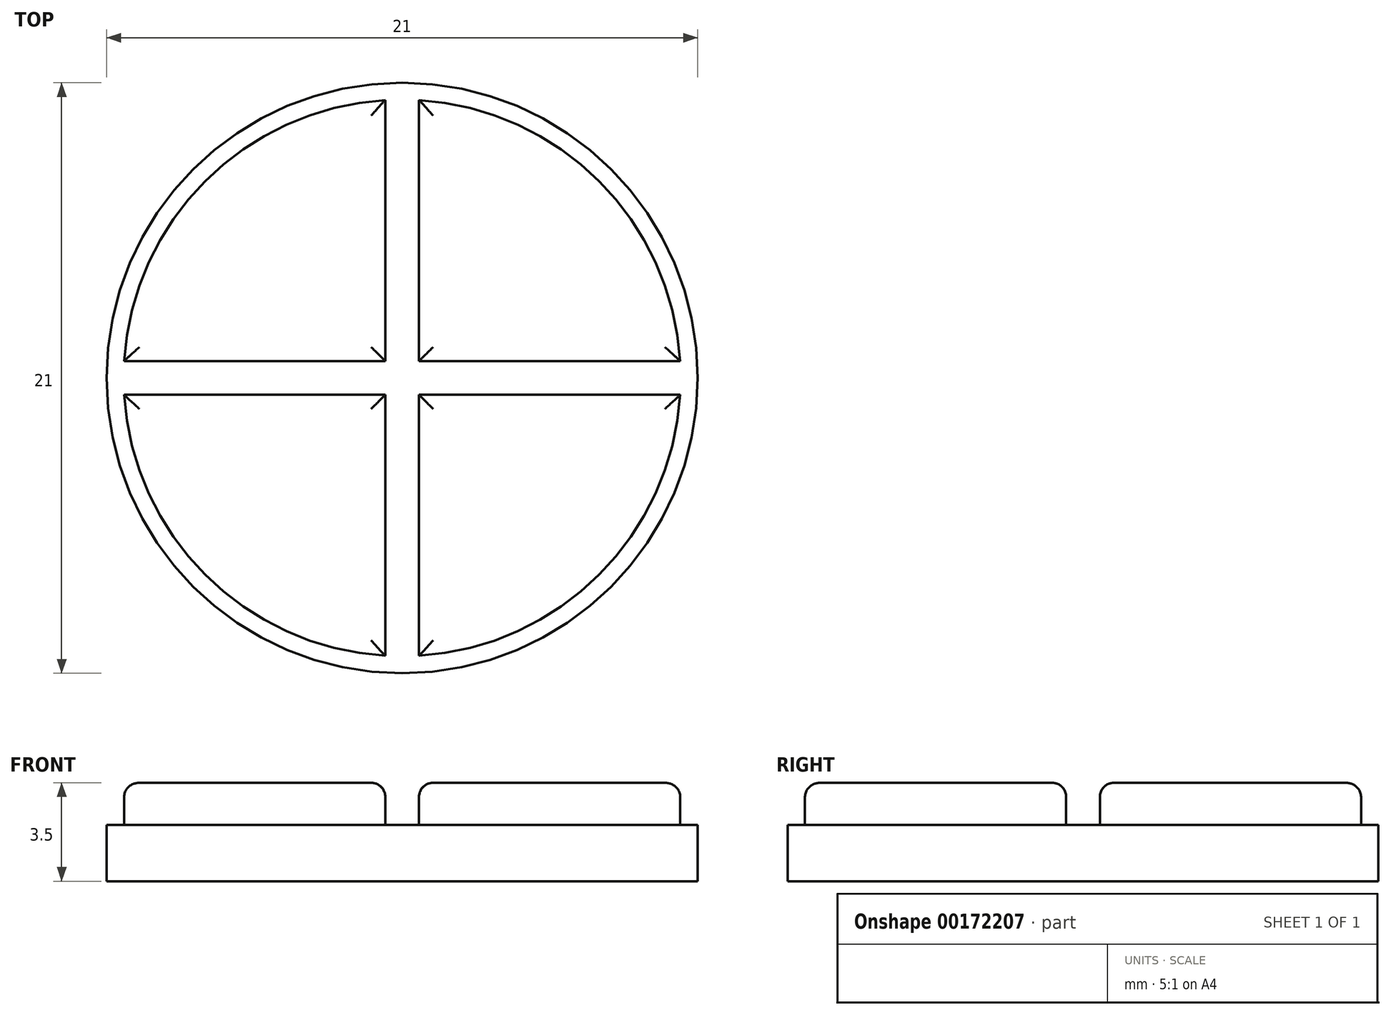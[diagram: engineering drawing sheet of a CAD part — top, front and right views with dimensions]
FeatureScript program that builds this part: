
annotation { "Feature Type Name" : "Feature", "Feature Type Description" : "" }
export const myFeature = defineFeature(function(context is Context, id is Id, definition is map)
    precondition{}
    {
        {
            var Q0;
            Q0=qCreatedBy(makeId("Top.planeOp"),FACE);
            var sketch = newSketch(context, id + "F0", { "sketchPlane" : qUnion([Q0])});
            skCircle(sketch, "E0", {"center": v(0, 0) * mm, "radius": 10.5 * mm});
            skSolve(sketch);
        }
        {
            var Q0;
            Q0=qSketchRegion(id+"F0",true);
            extrude(context, id + "F1", {"entities" : qUnion([Q0]), "depth" : 2 * mm});
        }
        {
            var Q0;
            Q0=makeQuery(id+"F1.opExtrude","CAP_FACE",FACE,{"disambiguationData":[OSD([sQuery(id+"F0.wireOp",EDGE,"E0")])],"isStart":false});
            var sketch = newSketch(context, id + "F2", { "sketchPlane" : qUnion([Q0])});
            skCircle(sketch, "E1", {"center": v(0, 0) * mm, "radius": 9.9 * mm});
            skLineSegment(sketch, "E2.bottom", {"start": v(9.88, -0.6) * mm, "end": v(-9.88, -0.6) * mm});
            skLineSegment(sketch, "E2.top", {"start": v(9.88, 0.6) * mm, "end": v(-9.88, 0.6) * mm});
            skLineSegment(sketch, "E2.left", {"start": v(9.88, -0.6) * mm, "end": v(9.88, 0.6) * mm});
            skLineSegment(sketch, "E2.right", {"start": v(-9.88, -0.6) * mm, "end": v(-9.88, 0.6) * mm});
            skLineSegment(sketch, "E3.bottom", {"start": v(0.6, -9.88) * mm, "end": v(-0.6, -9.88) * mm});
            skLineSegment(sketch, "E3.top", {"start": v(0.6, 9.88) * mm, "end": v(-0.6, 9.88) * mm});
            skLineSegment(sketch, "E3.left", {"start": v(0.6, -9.88) * mm, "end": v(0.6, 9.88) * mm});
            skLineSegment(sketch, "E3.right", {"start": v(-0.6, -9.88) * mm, "end": v(-0.6, 9.88) * mm});
            skSolve(sketch);
        }
        {
            var Q0;
            {var subQ0=sQuery(id+"F2.wireOp",EDGE,"E2.bottom");var subQ3=sQuery(id+"F2.wireOp",EDGE,"E3.right");var subQ5=makeQuery(id+"F2.imprint","INTERSECT",VERTEX,{"derivedFrom":[subQ0,subQ3]});Q0=makeQuery(id+"F2.imprint","IMPRINT",FACE,{"disambiguationData":[TD([[makeQuery(id+"F2.imprint","IMPRINT",EDGE,{"disambiguationData":[TD([[subQ5,-1.0]])],"derivedFrom":subQ0}),1.0]])]});}
            var Q1;
            {var subQ0=sQuery(id+"F2.wireOp",EDGE,"E2.top");var subQ3=sQuery(id+"F2.wireOp",EDGE,"E3.right");var subQ5=makeQuery(id+"F2.imprint","INTERSECT",VERTEX,{"derivedFrom":[subQ0,subQ3]});Q1=makeQuery(id+"F2.imprint","IMPRINT",FACE,{"disambiguationData":[TD([[makeQuery(id+"F2.imprint","IMPRINT",EDGE,{"disambiguationData":[TD([[subQ5,-1.0]])],"derivedFrom":subQ0}),-1.0]])]});}
            var Q2;
            {var subQ0=sQuery(id+"F2.wireOp",EDGE,"E2.top");var subQ3=sQuery(id+"F2.wireOp",EDGE,"E3.left");var subQ5=makeQuery(id+"F2.imprint","INTERSECT",VERTEX,{"derivedFrom":[subQ0,subQ3]});Q2=makeQuery(id+"F2.imprint","IMPRINT",FACE,{"disambiguationData":[TD([[makeQuery(id+"F2.imprint","IMPRINT",EDGE,{"disambiguationData":[TD([[subQ5,1.0]])],"derivedFrom":subQ0}),-1.0]])]});}
            var Q3;
            {var subQ0=sQuery(id+"F2.wireOp",EDGE,"E2.bottom");var subQ3=sQuery(id+"F2.wireOp",EDGE,"E3.left");var subQ5=makeQuery(id+"F2.imprint","INTERSECT",VERTEX,{"derivedFrom":[subQ0,subQ3]});Q3=makeQuery(id+"F2.imprint","IMPRINT",FACE,{"disambiguationData":[TD([[makeQuery(id+"F2.imprint","IMPRINT",EDGE,{"disambiguationData":[TD([[subQ5,1.0]])],"derivedFrom":subQ0}),1.0]])]});}
            extrude(context, id + "F3", {"entities" : qUnion([Q0, Q1, Q2, Q3]), "operationType" : NewBodyOperationType.ADD, "depth" : 1.5 * mm});
        }
        {
            var Q0;
            {var subQ0=sQuery(id+"F2.wireOp",EDGE,"E1");Q0=makeQuery(id+"F3.opExtrude","CAP_EDGE",EDGE,{"disambiguationData":[OSD([subQ0]),TDD([makeQuery(id+"F2.imprint","IMPRINT",EDGE,{"disambiguationData":[TD([[makeQuery(id+"F2.imprint","INTERSECT",VERTEX,{"derivedFrom":[subQ0,sQuery(id+"F2.wireOp",EDGE,"E2.bottom"),sQuery(id+"F2.wireOp",EDGE,"E2.right")]}),-1.0]])],"derivedFrom":subQ0})])],"isStart":false});}
            var Q1;
            {var subQ0=sQuery(id+"F2.wireOp",EDGE,"E3.right");Q1=makeQuery(id+"F3.opExtrude","CAP_EDGE",EDGE,{"disambiguationData":[OSD([subQ0]),TDD([makeQuery(id+"F2.imprint","IMPRINT",EDGE,{"disambiguationData":[TD([[makeQuery(id+"F2.imprint","INTERSECT",VERTEX,{"derivedFrom":[sQuery(id+"F2.wireOp",EDGE,"E2.bottom"),subQ0]}),1.0]])],"derivedFrom":subQ0})])],"isStart":false});}
            var Q2;
            {var subQ0=sQuery(id+"F2.wireOp",EDGE,"E2.bottom");Q2=makeQuery(id+"F3.opExtrude","CAP_EDGE",EDGE,{"disambiguationData":[OSD([subQ0]),TDD([makeQuery(id+"F2.imprint","IMPRINT",EDGE,{"disambiguationData":[TD([[makeQuery(id+"F2.imprint","INTERSECT",VERTEX,{"derivedFrom":[subQ0,sQuery(id+"F2.wireOp",EDGE,"E3.right")]}),-1.0]])],"derivedFrom":subQ0})])],"isStart":false});}
            var Q3;
            {var subQ0=sQuery(id+"F2.wireOp",EDGE,"E2.top");Q3=makeQuery(id+"F3.opExtrude","CAP_EDGE",EDGE,{"disambiguationData":[OSD([subQ0]),TDD([makeQuery(id+"F2.imprint","IMPRINT",EDGE,{"disambiguationData":[TD([[makeQuery(id+"F2.imprint","INTERSECT",VERTEX,{"derivedFrom":[subQ0,sQuery(id+"F2.wireOp",EDGE,"E3.right")]}),-1.0]])],"derivedFrom":subQ0})])],"isStart":false});}
            var Q4;
            {var subQ0=sQuery(id+"F2.wireOp",EDGE,"E3.right");Q4=makeQuery(id+"F3.opExtrude","CAP_EDGE",EDGE,{"disambiguationData":[OSD([subQ0]),TDD([makeQuery(id+"F2.imprint","IMPRINT",EDGE,{"disambiguationData":[TD([[makeQuery(id+"F2.imprint","INTERSECT",VERTEX,{"derivedFrom":[sQuery(id+"F2.wireOp",EDGE,"E2.top"),subQ0]}),-1.0]])],"derivedFrom":subQ0})])],"isStart":false});}
            var Q5;
            {var subQ0=sQuery(id+"F2.wireOp",EDGE,"E2.top");Q5=makeQuery(id+"F3.opExtrude","CAP_EDGE",EDGE,{"disambiguationData":[OSD([subQ0]),TDD([makeQuery(id+"F2.imprint","IMPRINT",EDGE,{"disambiguationData":[TD([[makeQuery(id+"F2.imprint","INTERSECT",VERTEX,{"derivedFrom":[subQ0,sQuery(id+"F2.wireOp",EDGE,"E3.left")]}),1.0]])],"derivedFrom":subQ0})])],"isStart":false});}
            var Q6;
            {var subQ0=sQuery(id+"F2.wireOp",EDGE,"E3.left");Q6=makeQuery(id+"F3.opExtrude","CAP_EDGE",EDGE,{"disambiguationData":[OSD([subQ0]),TDD([makeQuery(id+"F2.imprint","IMPRINT",EDGE,{"disambiguationData":[TD([[makeQuery(id+"F2.imprint","INTERSECT",VERTEX,{"derivedFrom":[sQuery(id+"F2.wireOp",EDGE,"E2.top"),subQ0]}),-1.0]])],"derivedFrom":subQ0})])],"isStart":false});}
            var Q7;
            {var subQ0=sQuery(id+"F2.wireOp",EDGE,"E2.bottom");Q7=makeQuery(id+"F3.opExtrude","CAP_EDGE",EDGE,{"disambiguationData":[OSD([subQ0]),TDD([makeQuery(id+"F2.imprint","IMPRINT",EDGE,{"disambiguationData":[TD([[makeQuery(id+"F2.imprint","INTERSECT",VERTEX,{"derivedFrom":[subQ0,sQuery(id+"F2.wireOp",EDGE,"E3.left")]}),1.0]])],"derivedFrom":subQ0})])],"isStart":false});}
            var Q8;
            {var subQ0=sQuery(id+"F2.wireOp",EDGE,"E3.left");Q8=makeQuery(id+"F3.opExtrude","CAP_EDGE",EDGE,{"disambiguationData":[OSD([subQ0]),TDD([makeQuery(id+"F2.imprint","IMPRINT",EDGE,{"disambiguationData":[TD([[makeQuery(id+"F2.imprint","INTERSECT",VERTEX,{"derivedFrom":[sQuery(id+"F2.wireOp",EDGE,"E2.bottom"),subQ0]}),1.0]])],"derivedFrom":subQ0})])],"isStart":false});}
            var Q9;
            {var subQ0=sQuery(id+"F2.wireOp",EDGE,"E1");Q9=makeQuery(id+"F3.opExtrude","CAP_EDGE",EDGE,{"disambiguationData":[OSD([subQ0]),TDD([makeQuery(id+"F2.imprint","IMPRINT",EDGE,{"disambiguationData":[TD([[makeQuery(id+"F2.imprint","INTERSECT",VERTEX,{"derivedFrom":[subQ0,sQuery(id+"F2.wireOp",EDGE,"E2.bottom"),sQuery(id+"F2.wireOp",EDGE,"E2.left")]}),1.0]])],"derivedFrom":subQ0})])],"isStart":false});}
            var Q10;
            {var subQ0=sQuery(id+"F2.wireOp",EDGE,"E1");Q10=makeQuery(id+"F3.opExtrude","CAP_EDGE",EDGE,{"disambiguationData":[OSD([subQ0]),TDD([makeQuery(id+"F2.imprint","IMPRINT",EDGE,{"disambiguationData":[TD([[makeQuery(id+"F2.imprint","INTERSECT",VERTEX,{"derivedFrom":[subQ0,sQuery(id+"F2.wireOp",EDGE,"E2.top"),sQuery(id+"F2.wireOp",EDGE,"E2.left")]}),-1.0]])],"derivedFrom":subQ0})])],"isStart":false});}
            var Q11;
            {var subQ0=sQuery(id+"F2.wireOp",EDGE,"E1");Q11=makeQuery(id+"F3.opExtrude","CAP_EDGE",EDGE,{"disambiguationData":[OSD([subQ0]),TDD([makeQuery(id+"F2.imprint","IMPRINT",EDGE,{"disambiguationData":[TD([[makeQuery(id+"F2.imprint","INTERSECT",VERTEX,{"derivedFrom":[subQ0,sQuery(id+"F2.wireOp",EDGE,"E2.top"),sQuery(id+"F2.wireOp",EDGE,"E2.right")]}),1.0]])],"derivedFrom":subQ0})])],"isStart":false});}
            fillet(context, id + "F4", {"entities" : qUnion([Q0, Q1, Q2, Q3, Q4, Q5, Q6, Q7, Q8, Q9, Q10, Q11]), "radius" : 0.5 * mm, "tangentPropagation" : true, "allowEdgeOverflow" : false});
        }
    });
